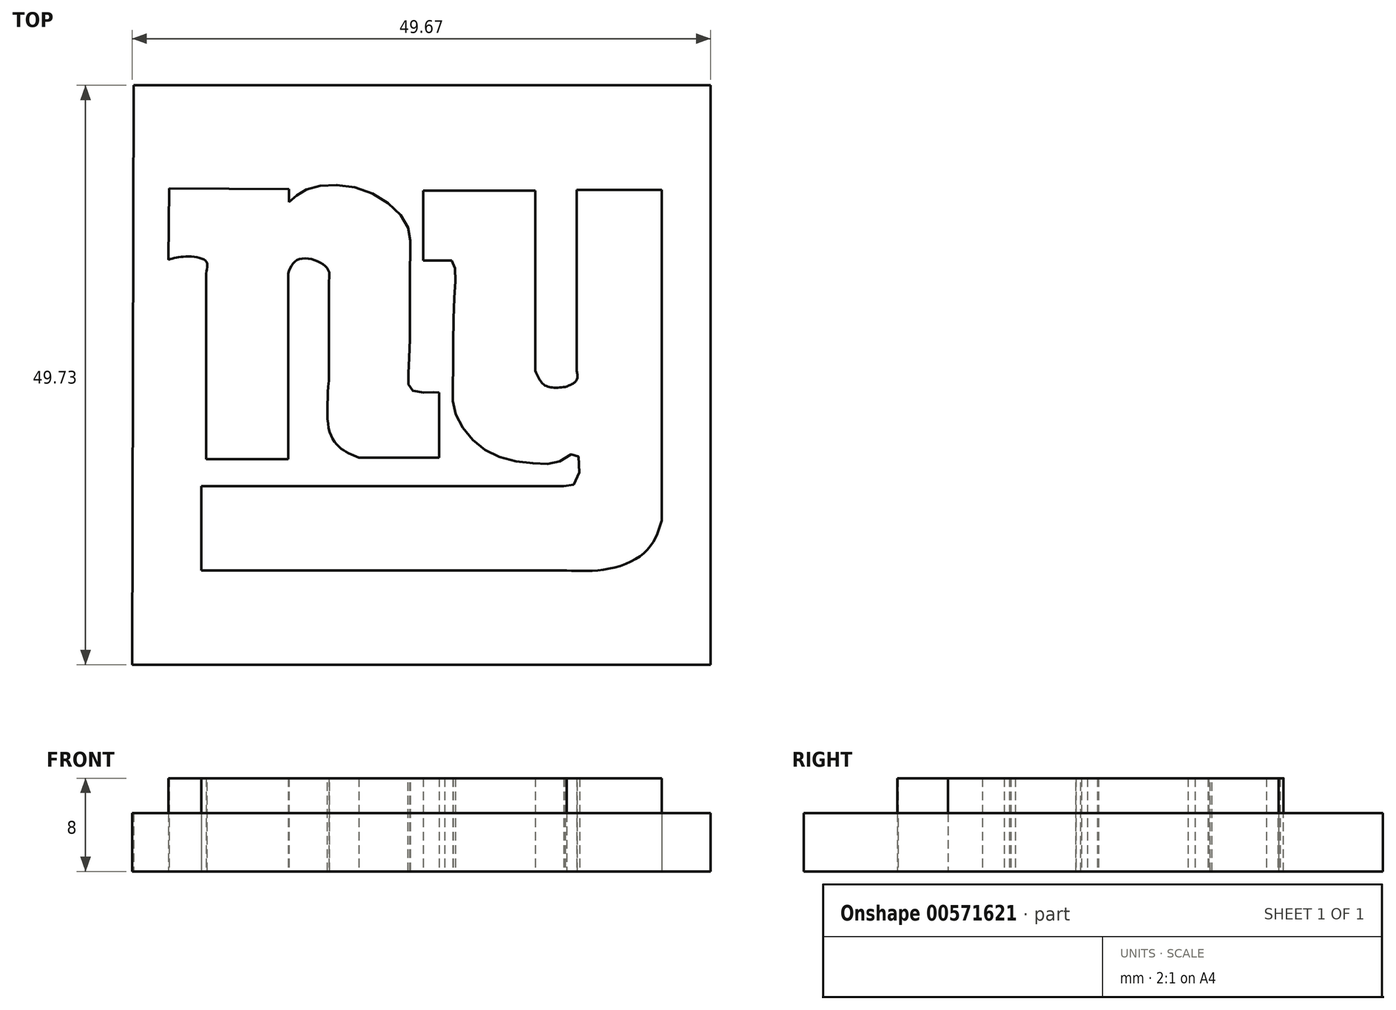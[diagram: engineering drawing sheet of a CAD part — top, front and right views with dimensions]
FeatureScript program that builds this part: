
annotation { "Feature Type Name" : "Feature", "Feature Type Description" : "" }
export const myFeature = defineFeature(function(context is Context, id is Id, definition is map)
    precondition{}
    {
        {
            var Q0;
            Q0=qCreatedBy(makeId("Top.planeOp"),FACE);
            var sketch = newSketch(context, id + "F0", { "sketchPlane" : qUnion([Q0])});
            skFitSpline(sketch, "E0", {"points": [v(5.15, 40.9) * mm, v(15.42, 40.83) * mm], "startDerivative": vector(10.28, -0.07) * mm, "endDerivative": vector(10.28, -0.07) * mm});
            skLineSegment(sketch, "E1", {"start": v(15.42, 40.83) * mm, "end": v(15.42, 39.7) * mm});
            skFitSpline(sketch, "E2", {"points": [v(15.42, 39.7) * mm, v(17.07, 40.83) * mm, v(21.62, 40.83) * mm, v(25.5, 37.86) * mm, v(25.83, 34.9) * mm, v(25.83, 30.48) * mm, v(25.7, 25.02) * mm, v(25.97, 23.57) * mm, v(27.74, 23.37) * mm, v(28.34, 23.37) * mm], "startDerivative": vector(14.67, 13.62) * mm, "endDerivative": vector(9.15, -0.24) * mm});
            skLineSegment(sketch, "E3", {"start": v(28.34, 23.37) * mm, "end": v(28.34, 17.77) * mm});
            skLineSegment(sketch, "E4", {"start": v(28.34, 17.77) * mm, "end": v(21.42, 17.77) * mm});
            skFitSpline(sketch, "E5", {"points": [v(21.42, 17.77) * mm, v(20.17, 18.36) * mm, v(18.98, 19.81) * mm, v(18.85, 24.36) * mm], "startDerivative": vector(-5.02, 1.96) * mm, "endDerivative": vector(0.84, 11.36) * mm});
            skLineSegment(sketch, "E6", {"start": v(18.85, 24.36) * mm, "end": v(18.85, 29.23) * mm});
            skLineSegment(sketch, "E7", {"start": v(18.85, 29.23) * mm, "end": v(18.85, 32.99) * mm});
            skFitSpline(sketch, "E8", {"points": [v(18.85, 32.99) * mm, v(18.85, 33.78) * mm, v(17.73, 34.7) * mm, v(16.08, 34.7) * mm, v(15.36, 33.58) * mm], "startDerivative": vector(0.82, 4.02) * mm, "endDerivative": vector(-2.06, -5.28) * mm});
            skLineSegment(sketch, "E9", {"start": v(15.36, 33.58) * mm, "end": v(15.36, 17.64) * mm});
            skLineSegment(sketch, "E10", {"start": v(15.36, 17.64) * mm, "end": v(8.3, 17.64) * mm});
            skLineSegment(sketch, "E11", {"start": v(8.3, 17.64) * mm, "end": v(8.3, 33.58) * mm});
            skFitSpline(sketch, "E12", {"points": [v(8.3, 33.58) * mm, v(8.3, 34.64) * mm, v(6.53, 35.03) * mm, v(5.08, 34.77) * mm], "startDerivative": vector(1.13, 4.19) * mm, "endDerivative": vector(-3.83, -1.06) * mm});
            skLineSegment(sketch, "E13", {"start": v(5.08, 34.77) * mm, "end": v(5.15, 40.9) * mm});
            skLineSegment(sketch, "E14", {"start": v(26.95, 40.7) * mm, "end": v(36.57, 40.7) * mm});
            skLineSegment(sketch, "E15", {"start": v(40.13, 40.76) * mm, "end": v(47.44, 40.76) * mm});
            skLineSegment(sketch, "E16", {"start": v(47.44, 40.76) * mm, "end": v(47.44, 12.37) * mm});
            skLineSegment(sketch, "E17", {"start": v(36.57, 40.7) * mm, "end": v(36.57, 25.21) * mm});
            skLineSegment(sketch, "E18", {"start": v(40.13, 40.76) * mm, "end": v(40.13, 25.28) * mm});
            skLineSegment(sketch, "E19", {"start": v(39.01, 15.33) * mm, "end": v(7.91, 15.33) * mm});
            skLineSegment(sketch, "E20", {"start": v(7.91, 15.33) * mm, "end": v(7.91, 8.08) * mm});
            skLineSegment(sketch, "E21", {"start": v(7.91, 8.08) * mm, "end": v(39.27, 8.08) * mm});
            skFitSpline(sketch, "E22", {"points": [v(36.57, 25.21) * mm, v(37.43, 23.96) * mm, v(39.14, 23.83) * mm], "startDerivative": vector(1.4, -3.15) * mm, "endDerivative": vector(3.72, 0.34) * mm});
            skFitSpline(sketch, "E23", {"points": [v(39.14, 23.83) * mm, v(40.13, 24.42) * mm, v(40.13, 25.28) * mm], "startDerivative": vector(2.33, 0.9) * mm, "endDerivative": vector(-0.43, 2.02) * mm});
            skFitSpline(sketch, "E24", {"points": [v(39.27, 8.08) * mm, v(41.84, 8.08) * mm, v(44.88, 8.88) * mm, v(46.65, 10.46) * mm, v(47.44, 12.37) * mm], "startDerivative": vector(9.82, -0.5) * mm, "endDerivative": vector(2.75, 8.75) * mm});
            skLineSegment(sketch, "E25", {"start": v(26.95, 40.7) * mm, "end": v(26.95, 34.7) * mm});
            skLineSegment(sketch, "E26", {"start": v(26.95, 34.7) * mm, "end": v(28.8, 34.7) * mm});
            skFitSpline(sketch, "E27", {"points": [v(28.8, 34.7) * mm, v(29.4, 34.7) * mm, v(29.72, 33.78) * mm, v(29.59, 30.62) * mm, v(29.52, 24.42) * mm, v(29.66, 21.79) * mm, v(31.04, 19.48) * mm, v(33.48, 17.84) * mm, v(36.84, 17.24) * mm, v(38.81, 17.5) * mm, v(40.13, 18.1) * mm, v(40.13, 15.73) * mm, v(39.01, 15.33) * mm], "startDerivative": vector(15.43, 3.4) * mm, "endDerivative": vector(-21.54, 0.82) * mm});
            skSolve(sketch);
        }
        {
            var Q0;
            Q0=qCreatedBy(makeId("Top.planeOp"),FACE);
            var sketch = newSketch(context, id + "F1", { "sketchPlane" : qUnion([Q0])});
            skLineSegment(sketch, "E28", {"start": v(2.1, 49.73) * mm, "end": v(51.64, 49.73) * mm});
            skLineSegment(sketch, "E29", {"start": v(51.64, 49.73) * mm, "end": v(51.64, 0) * mm});
            skLineSegment(sketch, "E30", {"start": v(51.64, 0) * mm, "end": v(1.97, 0) * mm});
            skLineSegment(sketch, "E31", {"start": v(1.97, 0) * mm, "end": v(2.1, 49.73) * mm});
            skSolve(sketch);
        }
        {
            var Q0;
            Q0=makeQuery(id+"F0.imprint","IMPRINT",FACE,{"disambiguationData":[TD([[makeQuery(id+"F0.imprint","IMPRINT",EDGE,{"derivedFrom":sQuery(id+"F0.wireOp",EDGE,"E0")}),-1.0]])]});
            var Q1;
            Q1=makeQuery(id+"F0.imprint","IMPRINT",FACE,{"disambiguationData":[TD([[makeQuery(id+"F0.imprint","IMPRINT",EDGE,{"derivedFrom":sQuery(id+"F0.wireOp",EDGE,"E14")}),-1.0]])]});
            extrude(context, id + "F2", {"entities" : qUnion([Q0, Q1]), "depth" : 8 * mm, "offsetDistance" : 25 * mm});
        }
        {
            var Q0;
            Q0=makeQuery(id+"F1.imprint","IMPRINT",FACE,{"disambiguationData":[TD([[makeQuery(id+"F1.imprint","IMPRINT",EDGE,{"derivedFrom":sQuery(id+"F1.wireOp",EDGE,"E28")}),-1.0]])]});
            extrude(context, id + "F3", {"entities" : qUnion([Q0]), "depth" : 5 * mm, "offsetDistance" : 25 * mm});
        }
    });
